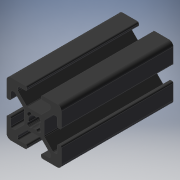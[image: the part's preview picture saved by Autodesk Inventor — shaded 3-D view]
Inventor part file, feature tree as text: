
AUTODESK INVENTOR PART (.ipt)
format: ipt  version: 2019 (Build 230136000, 136)  size: 235,008 bytes
history: native  units: mm
features: extrude x1, sketch x1
ambient origin geometry x8: Origin, YZ Plane, XZ Plane, XY Plane, X Axis, Y Axis, Z Axis, Center Point
bodies: Solid1 (feature_tree)
feature tree (2):
  extrude  "Extrusion1"  [1 undecoded]
  sketch  "Sketch_1"  dims[d0=41.0mm d1=0.0mm]
note: 1 required parameter value undecoded (feature->parameter linkage not recoverable at this tier; creation-order binding heuristic only, values carry confidence <= 0.55)
